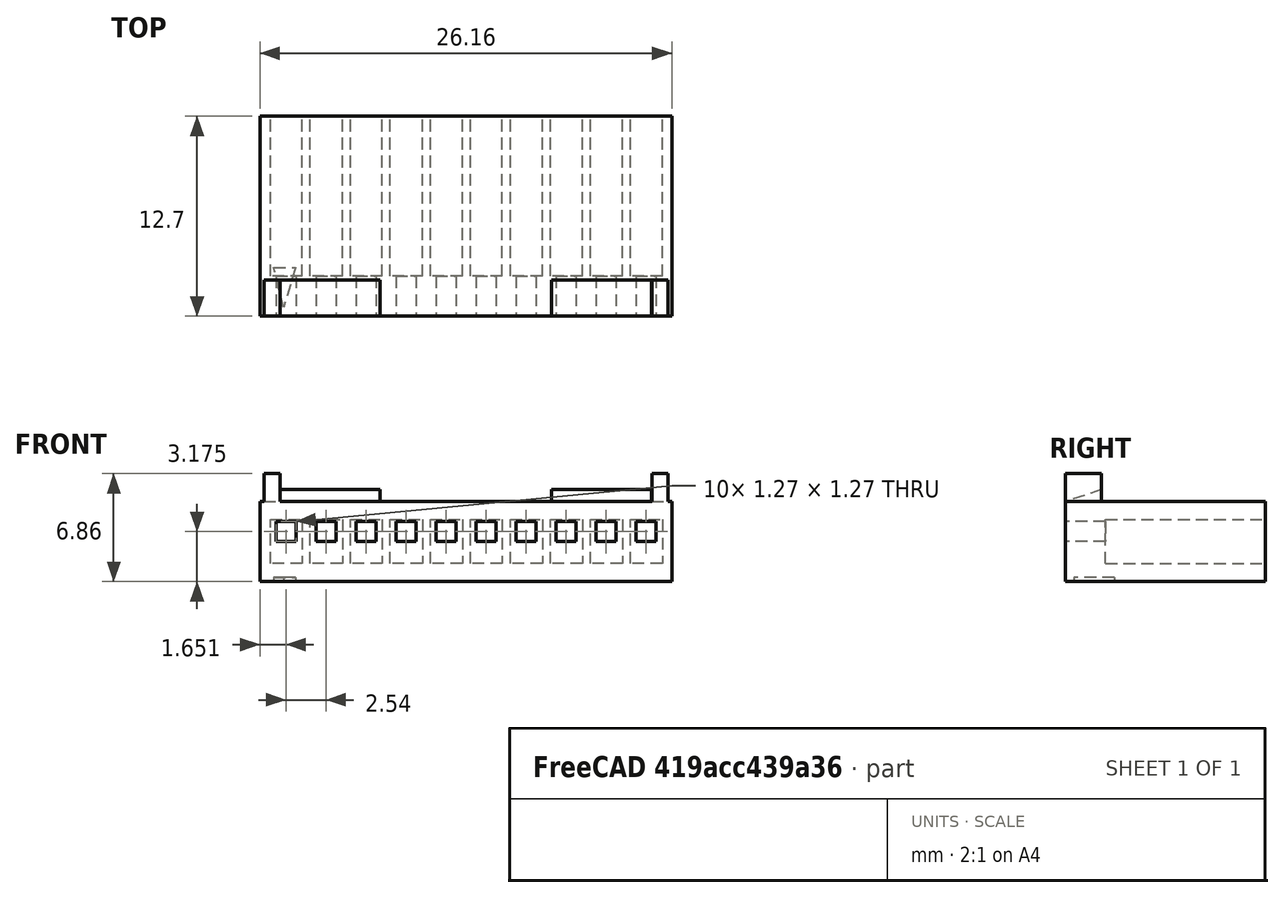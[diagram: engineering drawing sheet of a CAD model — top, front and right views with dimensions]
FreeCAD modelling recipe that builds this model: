
FCSTD DOCUMENT  (FreeCAD 0.18.4R)
Label: 0022013107
License: All rights reserved
LicenseURL: http://en.wikipedia.org/wiki/All_rights_reserved
objects: Part::Extrusion×9, Part::Part2DObjectPython×8, Part::Cut×5, Part::FeaturePython×2, Part::Mirroring×1, Part::MultiFuse×1, PartDesign::FeatureBase×1, PartDesign::Body×1
note: 28 computed .brp shape members not serialized (recipe doc carries the construction recipe); baked Part::Feature solids carry a one-line shape summary decoded from their .brp

FEATURE [Part::Part2DObjectPython] Rectangle  # Draft 2D object (typed FeaturePython)
  ChamferSize = 0
  Columns = 1
  FilletRadius = 0
  Height = 5.08
  Length = 26.162
  MakeFace = true
  Placement = pos=(0,0,0) rot=(1,0,0;1.5708rad)
  Rows = 1
FEATURE [Part::Part2DObjectPython] Rectangle001  # Draft 2D object (typed FeaturePython)
  ChamferSize = 0
  Columns = 1
  FilletRadius = 0
  Height = 1.778
  Length = 1.016
  MakeFace = true
  Placement = pos=(0.254,0,5.08) rot=(1,0,0;1.5708rad)
  Rows = 1
FEATURE [Part::Part2DObjectPython] Rectangle002  # Draft 2D object (typed FeaturePython)
  ChamferSize = 0
  Columns = 1
  FilletRadius = 0
  Height = 1.778
  Length = 1.016
  MakeFace = true
  Placement = pos=(24.892,-1.05977e-07,5.08) rot=(1,0,0;1.5708rad)
  Rows = 1
FEATURE [Part::Part2DObjectPython] Rectangle003  # Draft 2D object (typed FeaturePython)
  ChamferSize = 0
  Columns = 1
  FilletRadius = 0
  Height = 1.27
  Length = 1.27
  MakeFace = true
  Placement = pos=(1.016,0,2.54) rot=(1,0,0;1.5708rad)
  Rows = 1
FEATURE [Part::FeaturePython] Array  # Draft array (typed FeaturePython)
  Angle = 360
  ArrayType = 0
  Axis = (0,0,1)
  Base = -> Rectangle003
  Center = (0,0,0)
  Fuse = false
  IntervalAxis = (0,0,0)
  IntervalX = (2.54,0,0)
  IntervalY = (0,1,0)
  IntervalZ = (0,0,1)
  NumberPolar = 1
  NumberX = 10
  NumberY = 1
  NumberZ = 1
FEATURE [Part::Extrusion] Extrude
  Base = -> Rectangle001
  Dir = (0,-1,2.98023e-08)
  DirMode = 2
  FaceMakerClass = Part::FaceMakerBullseye
  LengthFwd = 0
  LengthRev = 2.286
  Solid = true
  Symmetric = false
FEATURE [Part::Extrusion] Extrude001
  Base = -> Rectangle002
  Dir = (0,-1,2e-16)
  DirMode = 2
  FaceMakerClass = Part::FaceMakerBullseye
  LengthFwd = 0
  LengthRev = 2.286
  Solid = true
  Symmetric = false
FEATURE [Part::Extrusion] Extrude002
  Base = -> Rectangle
  Dir = (0,-1,2.98023e-08)
  DirMode = 2
  FaceMakerClass = Part::FaceMakerBullseye
  LengthFwd = 0
  LengthRev = 12.7
  Solid = true
  Symmetric = false
FEATURE [Part::Extrusion] Extrude003
  Base = -> Array
  Dir = (0,-1,2e-16)
  DirMode = 2
  FaceMakerClass = Part::FaceMakerBullseye
  LengthFwd = 50.8
  LengthRev = 50.8
  Solid = true
  Symmetric = true
FEATURE [Part::Cut] Cut
  Base = -> Extrude002
  Tool = -> Extrude003
FEATURE [Part::Part2DObjectPython] Rectangle004  # Draft 2D object (typed FeaturePython)
  ChamferSize = 0
  Columns = 1
  FilletRadius = 0
  Height = 2.794
  Length = 2.032
  MakeFace = true
  Placement = pos=(0.6604,12.7,3.937) rot=(-1,0,0;1.5708rad)
  Rows = 1
  Support = -> [Cut]
FEATURE [Part::FeaturePython] Array001  # Draft array (typed FeaturePython)
  Angle = 360
  ArrayType = 0
  Axis = (0,0,1)
  Base = -> Rectangle004
  Center = (0,0,0)
  Fuse = false
  IntervalAxis = (0,0,0)
  IntervalX = (2.54,0,0)
  IntervalY = (0,1,0)
  IntervalZ = (0,0,1)
  NumberPolar = 1
  NumberX = 10
  NumberY = 1
  NumberZ = 1
FEATURE [Part::Extrusion] Extrude004
  Base = -> Array001
  Dir = (0,1,2e-16)
  DirMode = 2
  FaceMakerClass = Part::FaceMakerBullseye
  LengthFwd = 10.16
  LengthRev = 10.16
  Solid = true
  Symmetric = false
FEATURE [Part::Cut] Cut001
  Base = -> Cut
  Tool = -> Extrude004
FEATURE [Part::Part2DObjectPython] Rectangle005  # Draft 2D object (typed FeaturePython)
  ChamferSize = 0
  Columns = 1
  FilletRadius = 0
  Height = 2.286
  Length = -6.35
  MakeFace = true
  Placement = pos=(1.27,2.286,5.08) rot=(0,0,1;3.14159rad)
  Rows = 1
  Support = -> [Cut001]
FEATURE [Part::Mirroring] mirror  label="Mirror of Rectangle005"
  Base = (13.0729,9.12678,5.08)
  Normal = (-1,0,0)
  Source = -> Rectangle005
FEATURE [Part::Extrusion] Extrude005
  Base = -> Rectangle005
  Dir = (0,2.98024e-08,1)
  DirMode = 2
  FaceMakerClass = Part::FaceMakerBullseye
  LengthFwd = 0.762
  LengthRev = 0
  Solid = true
  Symmetric = false
FEATURE [Part::Extrusion] Extrude006
  Base = -> mirror
  Dir = (0,-2.98024e-08,-1)
  DirMode = 2
  FaceMakerClass = Part::FaceMakerBullseye
  LengthFwd = -0.762
  LengthRev = 0
  Solid = true
  Symmetric = false
FEATURE [Part::Part2DObjectPython] Wire  # Draft 2D object (typed FeaturePython)
  ChamferSize = 0
  Closed = true
  End = (7.62,2.286,5.842)
  FilletRadius = 0
  Length = 5.45361
  MakeFace = true
  Placement = pos=(7.62,9.15721e-11,5.08307) rot=(0.57735,0.57735,0.57735;2.0944rad)
  Points = (3) [(0,0,0),(4.43193e-16,0.758927,0),(2.286,0.758927,0)]
  Start = (7.62,9.15721e-11,5.08307)
  Subdivisions = 0
FEATURE [Part::Extrusion] Extrude007
  Base = -> Wire
  Dir = (1,-1e-16,3e-16)
  DirMode = 2
  FaceMakerClass = Part::FaceMakerBullseye
  LengthFwd = 17.272
  LengthRev = 6.35
  Solid = true
  Symmetric = false
FEATURE [Part::Cut] Cut002
  Base = -> Extrude005
  Tool = -> Extrude007
FEATURE [Part::Cut] Cut003
  Base = -> Extrude006
  Tool = -> Extrude007
FEATURE [Part::Part2DObjectPython] Wire002  # Draft 2D object (typed FeaturePython)
  ChamferSize = 0
  Closed = true
  End = (2.2691,3.1026,-9.24648e-08)
  FilletRadius = 0
  Length = 6.69756
  MakeFace = true
  Placement = pos=(1.49189,0.544275,-1.62207e-08) rot=(1,0,0;3.14159rad)
  Points = (3) [(0,0,0),(-0.615294,-2.55833,2.20473e-15),(0.777213,-2.55833,2.20473e-15)]
  Start = (1.49189,0.544275,-1.62207e-08)
  Subdivisions = 0
FEATURE [Part::Extrusion] Extrude008
  Base = -> Wire002
  Dir = (0,-2.98023e-08,-1)
  DirMode = 2
  FaceMakerClass = Part::FaceMakerBullseye
  LengthFwd = 0.254
  LengthRev = 0.254
  Solid = true
  Symmetric = false
FEATURE [Part::Cut] Cut004
  Base = -> Cut001
  Tool = -> Extrude008
FEATURE [Part::MultiFuse] Fusion
  Shapes = -> [Extrude,Extrude001,Cut002,Cut003,Cut004]
FEATURE [PartDesign::FeatureBase] BaseFeature
  BaseFeature = -> Fusion
FEATURE [PartDesign::Body] Body
  BaseFeature = -> Fusion
  Group = -> [BaseFeature]
  Origin = -> Origin
  Tip = -> BaseFeature
